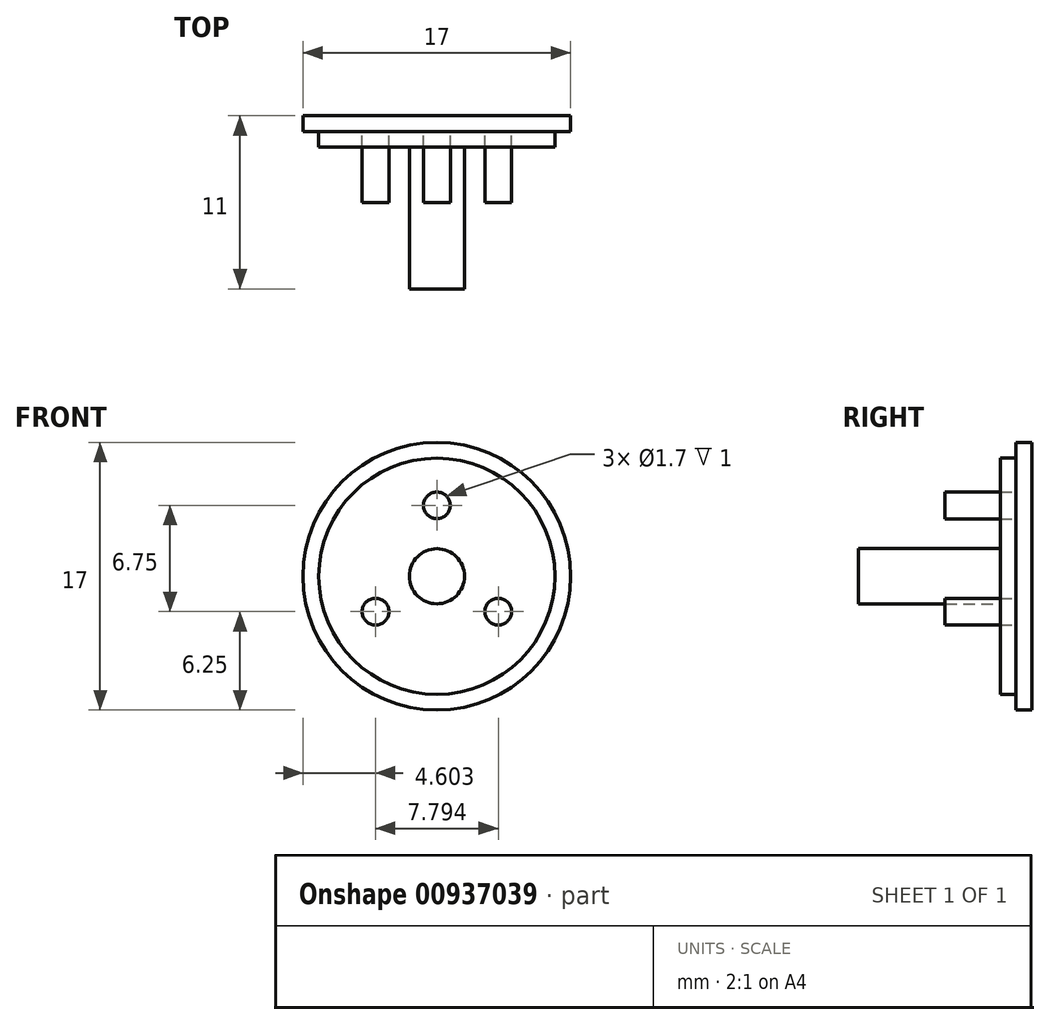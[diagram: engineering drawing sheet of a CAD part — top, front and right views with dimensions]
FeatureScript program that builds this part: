
annotation { "Feature Type Name" : "Feature", "Feature Type Description" : "" }
export const myFeature = defineFeature(function(context is Context, id is Id, definition is map)
    precondition{}
    {
        {
            var Q0;
            Q0=qCreatedBy(makeId("Front.planeOp"),FACE);
            var sketch = newSketch(context, id + "F0", { "sketchPlane" : qUnion([Q0])});
            skCircle(sketch, "E0", {"center": v(0, 4.5) * mm, "radius": 0.85 * mm});
            skPoint(sketch, "E1.center", {"position": v(0, 0) * mm});
            skCircle(sketch, "E2", {"center": v(0, 0) * mm, "radius": 7.5 * mm});
            skCircle(sketch, "E3", {"center": v(0, 0) * mm, "radius": 8.5 * mm});
            skCircle(sketch, "E4", {"center": v(0, 4.5) * mm, "radius": 2.5 * mm, "construction": true});
            skCircle(sketch, "E5.1.0", {"center": v(-3.9, -2.25) * mm, "radius": 0.85 * mm});
            skCircle(sketch, "E5.1.1", {"center": v(-3.9, -2.25) * mm, "radius": 2.5 * mm, "construction": true});
            skCircle(sketch, "E5.2.0", {"center": v(3.9, -2.25) * mm, "radius": 0.85 * mm});
            skCircle(sketch, "E5.2.1", {"center": v(3.9, -2.25) * mm, "radius": 2.5 * mm, "construction": true});
            skCircle(sketch, "E6", {"center": v(0, 0) * mm, "radius": 1.75 * mm});
            skSolve(sketch);
        }
        {
            var Q0;
            Q0=makeQuery(id+"F0.imprint","IMPRINT",FACE,{"disambiguationData":[TD([[makeQuery(id+"F0.imprint","IMPRINT",EDGE,{"derivedFrom":sQuery(id+"F0.wireOp",EDGE,"E0")}),1.0]])]});
            var Q1;
            Q1=makeQuery(id+"F0.imprint","IMPRINT",FACE,{"disambiguationData":[TD([[makeQuery(id+"F0.imprint","IMPRINT",EDGE,{"derivedFrom":sQuery(id+"F0.wireOp",EDGE,"E5.1.0")}),1.0]])]});
            var Q2;
            Q2=makeQuery(id+"F0.imprint","IMPRINT",FACE,{"disambiguationData":[TD([[makeQuery(id+"F0.imprint","IMPRINT",EDGE,{"derivedFrom":sQuery(id+"F0.wireOp",EDGE,"E5.2.0")}),1.0]])]});
            extrude(context, id + "F1", {"entities" : qUnion([Q0, Q1, Q2]), "depth" : 4.5 * mm, "offsetDistance" : 25 * mm});
        }
        {
            var Q0;
            Q0=makeQuery(id+"F0.imprint","IMPRINT",FACE,{"disambiguationData":[TD([[makeQuery(id+"F0.imprint","IMPRINT",EDGE,{"derivedFrom":sQuery(id+"F0.wireOp",EDGE,"E0")}),-1.0]])]});
            extrude(context, id + "F2", {"entities" : qUnion([Q0]), "depth" : 1 * mm, "offsetDistance" : 25 * mm});
        }
        {
            var Q0;
            Q0=makeQuery(id+"F0.imprint","IMPRINT",FACE,{"disambiguationData":[TD([[makeQuery(id+"F0.imprint","IMPRINT",EDGE,{"derivedFrom":sQuery(id+"F0.wireOp",EDGE,"E0")}),-1.0]])]});
            var Q1;
            Q1=makeQuery(id+"F0.imprint","IMPRINT",FACE,{"disambiguationData":[TD([[makeQuery(id+"F0.imprint","IMPRINT",EDGE,{"derivedFrom":sQuery(id+"F0.wireOp",EDGE,"E5.2.0")}),1.0]])]});
            var Q2;
            Q2=makeQuery(id+"F0.imprint","IMPRINT",FACE,{"disambiguationData":[TD([[makeQuery(id+"F0.imprint","IMPRINT",EDGE,{"derivedFrom":sQuery(id+"F0.wireOp",EDGE,"E5.1.0")}),1.0]])]});
            var Q3;
            Q3=makeQuery(id+"F0.imprint","IMPRINT",FACE,{"disambiguationData":[TD([[makeQuery(id+"F0.imprint","IMPRINT",EDGE,{"derivedFrom":sQuery(id+"F0.wireOp",EDGE,"E0")}),1.0]])]});
            var Q4;
            Q4=makeQuery(id+"F0.imprint","IMPRINT",FACE,{"disambiguationData":[TD([[makeQuery(id+"F0.imprint","IMPRINT",EDGE,{"derivedFrom":sQuery(id+"F0.wireOp",EDGE,"E2")}),-1.0]])]});
            var Q5;
            Q5=makeQuery(id+"F0.imprint","IMPRINT",FACE,{"disambiguationData":[TD([[makeQuery(id+"F0.imprint","IMPRINT",EDGE,{"derivedFrom":sQuery(id+"F0.wireOp",EDGE,"E6")}),1.0]])]});
            extrude(context, id + "F3", {"entities" : qUnion([Q0, Q1, Q2, Q3, Q4, Q5]), "oppositeDirection" : true, "depth" : 1 * mm, "offsetDistance" : 25 * mm});
        }
        {
            var Q0;
            Q0=makeQuery(id+"F0.imprint","IMPRINT",FACE,{"disambiguationData":[TD([[makeQuery(id+"F0.imprint","IMPRINT",EDGE,{"derivedFrom":sQuery(id+"F0.wireOp",EDGE,"E6")}),1.0]])]});
            extrude(context, id + "F4", {"entities" : qUnion([Q0]), "operationType" : NewBodyOperationType.ADD, "depth" : 10 * mm, "offsetDistance" : 25 * mm});
        }
    });
